# Revit family: 2014-ES_Puerta-Basculante-Contrapesada-Preleva-2-Hojas_AEPA_XXX
name_source: partatom
category: Puertas
revit_build: Autodesk Revit 2014 (Build: 20130308_1515(x64)
units: mm (PartAtom-declared; Revit-internal decimal feet)

## types (1)
- Puerta Garaje 3000x2600 mm
    Altura = 2600 mm  [stored 8.53018 ft]
    Altura CONTROL = 2600 mm  [stored 8.53018 ft]
    Altura dos tercios = 1733 mm
    Altura entre bisagras = 842 mm
    Altura_panel_inferior = 1728 mm
    Altura_panel_superior = 862 mm
    Anchura = 3000 mm
    Anchura CONTROL = 3000 mm
    Angulo de giro APERTURA = 60.00°
    Angulo de giro CONTROL = 60.00°
    Angulo de giro inferior = 120.00°
    Asociación - AEPA = http://www.aepa.ws
    Bimetica = http://www.bimetica.com
    Cierre de muro = Por anfitrión
    Colección = Biblioteca BIM AEPA
    Creado por = Bimetica Parametric Design Services S.L.
    Descripción = Puerta Basculante Contrapesada Prelevas 2 Hojas
    Fabricante - PUERTAS BAHÍA = http://www.puertasbahia.com
    Fabricante - ROLLTORE PORTIS = http://www.portis.es
    Fecha Revisión de Contenido = 19/12/2014
    Fecha de Caducidad de Información = 01/01/2016
    Función = Interior
    Grosor = 200 mm  [stored 0.656168 ft]
    Masterformat Código = 08 35 13
    Masterformat Descripción = Folding Doors
    Material de acabado = Panel Sandwich- Puerta Generica- AEPA
    Material estructura Acero = Acero - Puerta Generica - AEPA
    Material estructura Aluminio = Aluminio- Puerta Generica- AEPA
    Modelo = Genérico AEPA
    Omniclass Código = 23-17 11 19 15
    Omniclass Título = Folding Composite Doors
    UNSPSC Categoría = Folding door
    UNSPSC Código = 30171526
    URL = http://www.aepa.ws
    Uniclass 2.0 Código = 30-59-33-31
    Uniclass 2.0 Descripción = Folding gate automation mechanisms

note: [stored X ft] marks values corroborated as IEEE doubles in the binary element streams (Revit-internal decimal feet)
